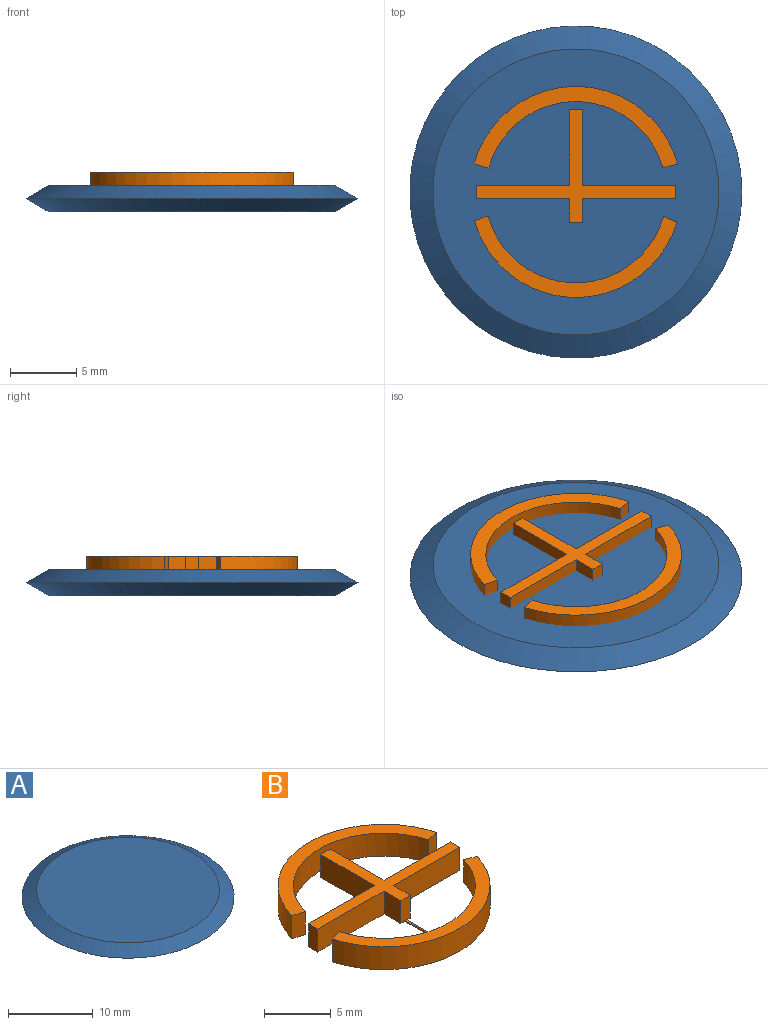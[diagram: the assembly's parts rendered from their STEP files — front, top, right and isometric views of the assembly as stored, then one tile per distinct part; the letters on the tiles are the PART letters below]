
ASSEMBLY  parts=2 mates=1
PART A: 4 faces, bbox 25x25x2 mm
  f0: plane 21.54x21.54mm, normal (0,0,1), area 364.3mm2, adj f1
  f1: cone r=12.5mm half-angle=60deg, axis (0,0,-1), area 146.2mm2, adj f0,f2
  f2: cone r=12.5mm half-angle=60deg, axis (0,0,1), area 146.2mm2, adj f1,f3
  f3: plane 21.54x21.54mm, normal (0,0,-1), area 364.3mm2, adj f2
PART B: 30 faces, bbox 15.3x15.9x2.1 mm
  f0: plane 0.59x0.1mm, normal (1,0,0), area 0.1mm2, adj f9,f25,f27,f28
  f1: plane 0.59x0.1mm, normal (-1,0,0), area 0.1mm2, adj f9,f25,f27,f28
  f2: plane 4.56x0.1mm, normal (-1,0,0), area 0.5mm2, adj f15,f16,f27,f29
  f3: plane 4.56x0.1mm, normal (1,0,0), area 0.5mm2, adj f15,f16,f27,f29
  f4: plane 15.25x6.11mm, normal (0,0,1), area 20.9mm2, adj f16,f17,f18,f19
  f5: plane 15x8.5mm, normal (0,0,1), area 22.5mm2, adj f10,f11,f12,f13,f14,f15,f20,f21
  f6: plane 2.1x1.12mm, normal (0.23,-0.97,0), area 2.4mm2, adj f7,f9,f26,f27
  f7: cylinder r=7.94mm len=15.32mm, axis (0,0,-1), area 43.5mm2, adj f6,f8,f26,f27
  f8: plane 2.1x1.1mm, normal (-0.27,-0.96,0), area 2.4mm2, adj f7,f9,f26,f27
  f9: cylinder r=6.8mm len=13.1mm, axis (0,0,-1), area 37.1mm2, adj f0,f1,f6,f8,f26,f27,f28
  f10: plane 5.71x2.1mm, normal (-1,0,0), area 12mm2, adj f5,f11,f25,f27
  f11: plane 7x2.1mm, normal (0,1,0), area 14.7mm2, adj f5,f10,f12,f27
  f12: plane 2.1x1mm, normal (-1,0,0), area 2.1mm2, adj f5,f11,f13,f27
  f13: plane 7x2.1mm, normal (0,-1,0), area 14.7mm2, adj f5,f12,f14,f27
  f14: plane 2.1x1.79mm, normal (-1,0,0), area 3.8mm2, adj f5,f13,f15,f27
  f15: plane 2.1x1mm, normal (0,-1,0), area 2.1mm2, adj f2,f3,f5,f14,f20,f27,f29
  f16: cylinder r=6.85mm len=13.19mm, axis (0,0,-1), area 37.3mm2, adj f2,f3,f4,f17,f19,f27,f29
  f17: plane 2.1x1.04mm, normal (-0.31,0.95,0), area 2.3mm2, adj f4,f16,f18,f27
  f18: cylinder r=7.94mm len=15.25mm, axis (0,0,-1), area 43mm2, adj f4,f17,f19,f27
  f19: plane 2.1x1.02mm, normal (0.37,0.93,0), area 2.3mm2, adj f4,f16,f18,f27
  f20: plane 2.1x1.79mm, normal (1,0,0), area 3.8mm2, adj f5,f15,f21,f27
  f21: plane 7x2.1mm, normal (0,-1,0), area 14.7mm2, adj f5,f20,f22,f27
  f22: plane 2.1x1mm, normal (1,0,0), area 2.1mm2, adj f5,f21,f23,f27
  f23: plane 7x2.1mm, normal (0,1,0), area 14.7mm2, adj f5,f22,f24,f27
  f24: plane 5.71x2.1mm, normal (1,0,0), area 12mm2, adj f5,f23,f25,f27
  f25: plane 2.1x1mm, normal (0,1,0), area 2.1mm2, adj f0,f1,f5,f10,f24,f27,f28
  f26: plane 15.32x6.16mm, normal (0,0,1), area 22mm2, adj f6,f7,f8,f9
  f27: plane 15.88x15.32mm, normal (0,0,-1), area 66.3mm2, adj f0,f1,f2,f3,f6,f7,f8,f9
  f28: plane 0.59x0.18mm, normal (0,0,1), area 0.1mm2, adj f0,f1,f9,f25
  f29: plane 4.56x0.16mm, normal (0,0,1), area 0.7mm2, adj f2,f3,f15,f16
PLACE A t=(-0.01,0.02,0.03)mm
PLACE B t=(-0.01,0.02,0.03)mm
MATE fastened B.f16 <-> A.f1  axis (0,0,-1) through (-0.01,0.02,-0.97)mm
